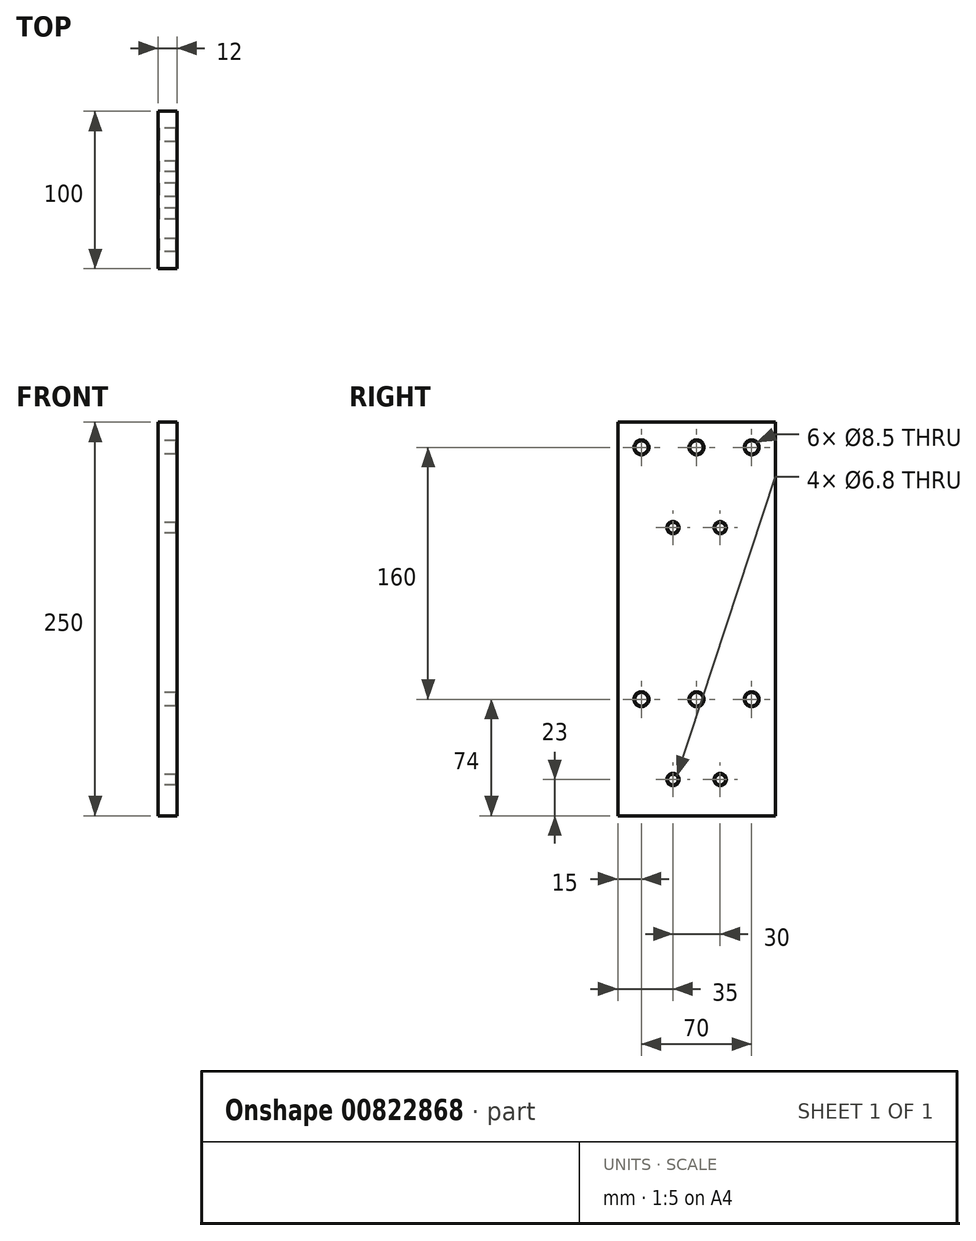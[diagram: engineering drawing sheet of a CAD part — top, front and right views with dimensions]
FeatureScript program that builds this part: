
annotation { "Feature Type Name" : "Feature", "Feature Type Description" : "" }
export const myFeature = defineFeature(function(context is Context, id is Id, definition is map)
    precondition{}
    {
        {
            var Q0;
            Q0=qCreatedBy(makeId("Right.planeOp"),FACE);
            var sketch = newSketch(context, id + "F0", { "sketchPlane" : qUnion([Q0])});
            skLineSegment(sketch, "E0.bottom", {"start": v(-50, 125) * mm, "end": v(50, 125) * mm});
            skLineSegment(sketch, "E0.top", {"start": v(-50, -125) * mm, "end": v(50, -125) * mm});
            skLineSegment(sketch, "E0.left", {"start": v(-50, 125) * mm, "end": v(-50, -125) * mm});
            skLineSegment(sketch, "E0.right", {"start": v(50, 125) * mm, "end": v(50, -125) * mm});
            skPoint(sketch, "E0.middle", {"position": v(0, 0) * mm});
            skLineSegment(sketch, "E1", {"start": v(0, 0) * mm, "end": v(0, 109) * mm, "construction": true});
            skLineSegment(sketch, "E2", {"start": v(0, 109) * mm, "end": v(-35, 109) * mm, "construction": true});
            skCircle(sketch, "E3", {"center": v(-35, 109) * mm, "radius": 4.25 * mm});
            skCircle(sketch, "E4", {"center": v(0, 109) * mm, "radius": 4.25 * mm});
            skCircle(sketch, "E5.MirrorC", {"center": v(35, 109) * mm, "radius": 4.25 * mm});
            skCircle(sketch, "E6.0.1.0", {"center": v(-35, -51) * mm, "radius": 4.25 * mm});
            skLineSegment(sketch, "E6.direction1", {"start": v(-35, 109) * mm, "end": v(-11.08, 109) * mm, "construction": true});
            skLineSegment(sketch, "E6.direction2", {"start": v(-35, 109) * mm, "end": v(-35, -51) * mm, "construction": true});
            skLineSegment(sketch, "E7", {"start": v(35, 109) * mm, "end": v(35, -51) * mm, "construction": true});
            skLineSegment(sketch, "E8", {"start": v(35, -51) * mm, "end": v(-35, -51) * mm, "construction": true});
            skCircle(sketch, "E9", {"center": v(35, -51) * mm, "radius": 4.25 * mm});
            skCircle(sketch, "E10", {"center": v(0, -51) * mm, "radius": 4.25 * mm});
            skCircle(sketch, "E11", {"center": v(-15, 58) * mm, "radius": 3.4 * mm});
            skCircle(sketch, "E12", {"center": v(-15, -102) * mm, "radius": 3.4 * mm});
            skCircle(sketch, "E13.MirrorC", {"center": v(15, -102) * mm, "radius": 3.4 * mm});
            skCircle(sketch, "E14.MirrorC", {"center": v(15, 58) * mm, "radius": 3.4 * mm});
            skSolve(sketch);
        }
        {
            var Q0;
            Q0 = qSketchRegion(id + "F0", true);
            extrude(context, id + "F1", {"entities" : qUnion([Q0]), "endBound" : BoundingType.SYMMETRIC, "depth" : 12 * mm, "offsetDistance" : 25 * mm});
        }
        {
            var Q0;
            Q0=makeQuery(id+"F1.opExtrude","SWEPT_FACE",FACE,{"disambiguationData":[OSD([sQuery(id+"F0.wireOp",EDGE,"E3")])]});
            var Q1;
            Q1=makeQuery(id+"F1.opExtrude","SWEPT_FACE",FACE,{"disambiguationData":[OSD([sQuery(id+"F0.wireOp",EDGE,"E4")])]});
            var Q2;
            Q2=makeQuery(id+"F1.opExtrude","SWEPT_FACE",FACE,{"disambiguationData":[OSD([sQuery(id+"F0.wireOp",EDGE,"E5.MirrorC")])]});
            var Q3;
            Q3=makeQuery(id+"F1.opExtrude","SWEPT_FACE",FACE,{"disambiguationData":[OSD([sQuery(id+"F0.wireOp",EDGE,"E9")])]});
            var Q4;
            Q4=makeQuery(id+"F1.opExtrude","SWEPT_FACE",FACE,{"disambiguationData":[OSD([sQuery(id+"F0.wireOp",EDGE,"E10")])]});
            var Q5;
            Q5=makeQuery(id+"F1.opExtrude","SWEPT_FACE",FACE,{"disambiguationData":[OSD([sQuery(id+"F0.wireOp",EDGE,"E6.0.1.0")])]});
            var Q6;
            Q6=makeQuery(id+"F1.opExtrude","SWEPT_FACE",FACE,{"disambiguationData":[OSD([sQuery(id+"F0.wireOp",EDGE,"E11")])]});
            var Q7;
            Q7=makeQuery(id+"F1.opExtrude","SWEPT_FACE",FACE,{"disambiguationData":[OSD([sQuery(id+"F0.wireOp",EDGE,"E14.MirrorC")])]});
            var Q8;
            Q8=makeQuery(id+"F1.opExtrude","SWEPT_FACE",FACE,{"disambiguationData":[OSD([sQuery(id+"F0.wireOp",EDGE,"E12")])]});
            var Q9;
            Q9=makeQuery(id+"F1.opExtrude","SWEPT_FACE",FACE,{"disambiguationData":[OSD([sQuery(id+"F0.wireOp",EDGE,"E13.MirrorC")])]});
            chamfer(context, id + "F2", {"entities" : qUnion([Q0, Q1, Q2, Q3, Q4, Q5, Q6, Q7, Q8, Q9]), "width" : 0.5 * mm, "tangentPropagation" : true});
        }
    });
